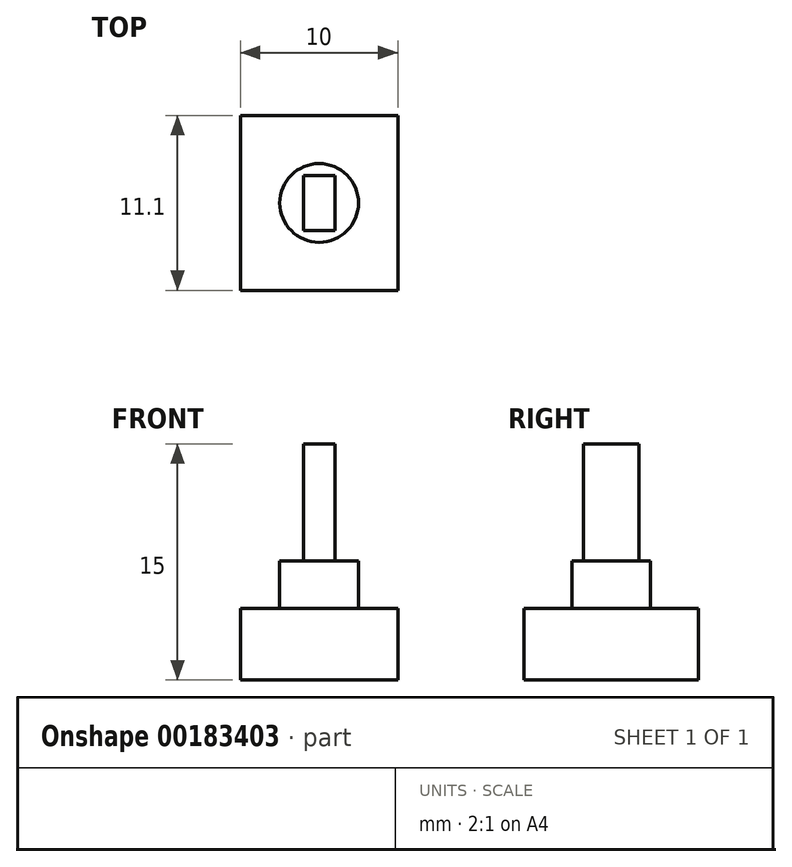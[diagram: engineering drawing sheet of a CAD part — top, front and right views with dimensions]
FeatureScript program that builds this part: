
annotation { "Feature Type Name" : "Feature", "Feature Type Description" : "" }
export const myFeature = defineFeature(function(context is Context, id is Id, definition is map)
    precondition{}
    {
        {
            var Q0;
            Q0=qCreatedBy(makeId("Top.planeOp"),FACE);
            var sketch = newSketch(context, id + "F0", { "sketchPlane" : qUnion([Q0])});
            skLineSegment(sketch, "E0.bottom", {"start": v(5, -5.55) * mm, "end": v(-5, -5.55) * mm});
            skLineSegment(sketch, "E0.top", {"start": v(5, 5.55) * mm, "end": v(-5, 5.55) * mm});
            skLineSegment(sketch, "E0.left", {"start": v(5, -5.55) * mm, "end": v(5, 5.55) * mm});
            skLineSegment(sketch, "E0.right", {"start": v(-5, -5.55) * mm, "end": v(-5, 5.55) * mm});
            skPoint(sketch, "E0.middle", {"position": v(0, 0) * mm});
            skSolve(sketch);
        }
        {
            var Q0;
            Q0 = qSketchRegion(id + "F0", true);
            extrude(context, id + "F1", {"entities" : qUnion([Q0]), "depth" : 4.55 * mm});
        }
        {
            var Q0;
            Q0=makeQuery(id+"F1.opExtrude","CAP_FACE",FACE,{"disambiguationData":[OSD([sQuery(id+"F0.wireOp",EDGE,"E0.bottom"),sQuery(id+"F0.wireOp",EDGE,"E0.top"),sQuery(id+"F0.wireOp",EDGE,"E0.left"),sQuery(id+"F0.wireOp",EDGE,"E0.right")])],"isStart":false});
            var sketch = newSketch(context, id + "F2", { "sketchPlane" : qUnion([Q0])});
            skCircle(sketch, "E1", {"center": v(0, 0) * mm, "radius": 2.5 * mm});
            skSolve(sketch);
        }
        {
            var Q0;
            Q0 = qSketchRegion(id + "F2", true);
            extrude(context, id + "F3", {"entities" : qUnion([Q0]), "operationType" : NewBodyOperationType.ADD, "depth" : 3 * mm});
        }
        {
            var Q0;
            Q0=makeQuery(id+"F3.opExtrude","CAP_FACE",FACE,{"disambiguationData":[OSD([sQuery(id+"F2.wireOp",EDGE,"E1")])],"isStart":false});
            var sketch = newSketch(context, id + "F4", { "sketchPlane" : qUnion([Q0])});
            skLineSegment(sketch, "E2.bottom", {"start": v(1, 1.75) * mm, "end": v(-1, 1.75) * mm});
            skLineSegment(sketch, "E2.top", {"start": v(1, -1.75) * mm, "end": v(-1, -1.75) * mm});
            skLineSegment(sketch, "E2.left", {"start": v(1, 1.75) * mm, "end": v(1, -1.75) * mm});
            skLineSegment(sketch, "E2.right", {"start": v(-1, 1.75) * mm, "end": v(-1, -1.75) * mm});
            skPoint(sketch, "E2.middle", {"position": v(0, 0) * mm});
            skSolve(sketch);
        }
        {
            var Q0;
            Q0 = qSketchRegion(id + "F4", true);
            extrude(context, id + "F5", {"entities" : qUnion([Q0]), "operationType" : NewBodyOperationType.ADD, "depth" : 7.45 * mm});
        }
    });
